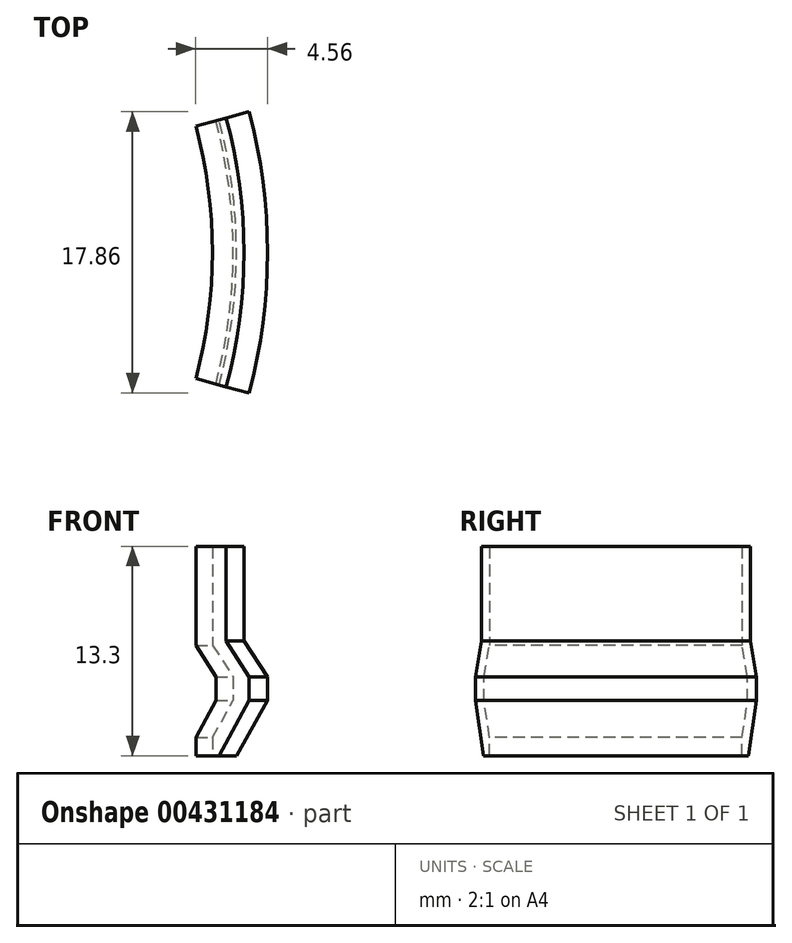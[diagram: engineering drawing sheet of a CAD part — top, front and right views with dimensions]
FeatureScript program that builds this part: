
annotation { "Feature Type Name" : "Feature", "Feature Type Description" : "" }
export const myFeature = defineFeature(function(context is Context, id is Id, definition is map)
    precondition{}
    {
        {
            var Q0;
            Q0=qCreatedBy(makeId("Front.planeOp"),FACE);
            var sketch = newSketch(context, id + "F0", { "sketchPlane" : qUnion([Q0])});
            skLineSegment(sketch, "E0", {"start": v(-1.53, 13.4) * mm, "end": v(-1.53, -16.7) * mm, "construction": true});
            skLineSegment(sketch, "E1", {"start": v(-5.34, -13.44) * mm, "end": v(7.52, -13.44) * mm, "construction": true});
            skLineSegment(sketch, "E2", {"start": v(1.97, -0.14) * mm, "end": v(1.97, -6.14) * mm, "construction": true});
            skLineSegment(sketch, "E3", {"start": v(-1.53, -0.14) * mm, "end": v(-1.53, -6.14) * mm});
            skLineSegment(sketch, "E4", {"start": v(-1.53, -0.14) * mm, "end": v(0.47, -0.14) * mm});
            skLineSegment(sketch, "E5", {"start": v(0.47, -0.14) * mm, "end": v(0.47, -6.14) * mm});
            skLineSegment(sketch, "E6", {"start": v(0.47, -6.14) * mm, "end": v(1.97, -8.43) * mm});
            skLineSegment(sketch, "E7", {"start": v(1.97, -8.43) * mm, "end": v(1.97, -9.93) * mm});
            skLineSegment(sketch, "E8", {"start": v(1.97, -9.93) * mm, "end": v(0, -13.44) * mm});
            skLineSegment(sketch, "E9", {"start": v(-1.53, -13.44) * mm, "end": v(-1.53, -12.28) * mm});
            skLineSegment(sketch, "E10", {"start": v(-1.53, -12.28) * mm, "end": v(-0.21, -9.93) * mm});
            skLineSegment(sketch, "E11", {"start": v(-0.21, -9.93) * mm, "end": v(-0.21, -8.43) * mm});
            skLineSegment(sketch, "E12", {"start": v(-0.21, -8.43) * mm, "end": v(-1.53, -6.42) * mm});
            skLineSegment(sketch, "E13", {"start": v(-1.53, -12.28) * mm, "end": v(-1.53, -13.44) * mm});
            skLineSegment(sketch, "E14", {"start": v(0, -13.44) * mm, "end": v(-1.53, -13.44) * mm});
            skLineSegment(sketch, "E15", {"start": v(-1.53, -6.14) * mm, "end": v(-1.53, -6.42) * mm});
            skLineSegment(sketch, "E16", {"start": v(-32.53, -36.24) * mm, "end": v(-32.53, 32.87) * mm, "construction": true});
            skLineSegment(sketch, "E17", {"start": v(-0.27, 2.36) * mm, "end": v(1.62, 2.36) * mm, "construction": true});
            skLineSegment(sketch, "E18", {"start": v(-1.53, -0.14) * mm, "end": v(1.97, -0.14) * mm});
            skLineSegment(sketch, "E19", {"start": v(9.26, 6.76) * mm, "end": v(9.47, 6.76) * mm});
            skLineSegment(sketch, "E20", {"start": v(-32.53, 5.76) * mm, "end": v(-32.53, 3.26) * mm});
            skLineSegment(sketch, "E21", {"start": v(45.47, 25.02) * mm, "end": v(45.47, 27.57) * mm});
            skSolve(sketch);
        }
        {
            var Q0;
            {var subQ0=sQuery(id+"F0.wireOp",EDGE,"E3");Q0=makeQuery(id+"F0.imprint","IMPRINT",FACE,{"disambiguationData":[TD([[makeQuery(id+"F0.imprint","IMPRINT",EDGE,{"derivedFrom":subQ0}),1.0]])]});}
            var Q1;
            Q1=sQuery(id+"F0.wireOp",EDGE,"E16");
            revolve(context, id + "F1", {"entities" : qUnion([Q0]), "axis" : qUnion([Q1]), "revolveType" : RevolveType.SYMMETRIC, "angle" : 30 * degree});
        }
    });
